# Revit family: QF_COMENDA_601682 AA_601682DDPS AA_CAT
name_source: partatom
category: Attrezzature speciali
units: mm (PartAtom-declared; Revit-internal decimal feet)

## family parameters
Basato su piano di lavoro = No
Condiviso = No
Numero OmniClass = 23.40.40.14
Punto di calcolo locali = No
Quota connettore circolare = Usa diametro
Sempre verticale = Sì
Taglio con vuoti quando caricato = No
Tipo di parte = Normale
Titolo OmniClass = Food Service Equipment

## types (3) — shared parameters
Altezza = 1960 mm  [stored 6.43045 ft]
Altezza allacciamento elettrico da pavimento finito = 360 mm
Altezza da terra raccordo acqua calda = 225 mm
Altezza dello scarico diretto acqua da pavimento finito = 225 mm
Corrente di funzionamento normale = 12 A
Diametro dello scarico diretto di acqua = 1 1/2"
Diametro raccordo acqua calda = 1"
Fase = 3
Frequenza = 50 Hz
Lunghezza = 620 mm  [stored 2.03412 ft]
Numero dei poli = 3
Peso netto = 0.00 kg
Potenza elettrica = 7500 W
Pressione minima acqua calda = 2000.0 Pa
Produttore = COMENDA
Profondità = 742 mm  [stored 2.43438 ft]
Protezione contro le sovracorrenti = 16 A
Temperatura raccomandata per acqua calda = 50 °C
Tensione = 400 V
URL = www.comenda.eu
zero-valued in all types: Prospetto di default

## per-type parameters (varying)
| type | Descrizione | Modello | URL catalogo |
| 601690/AA | MULTIPURPOSE WASHER 500X600 MM RACK SIZE WITH CRC | PFS90 R CRC |  |
| 601690DDPS/AA | MULTIPURPOSE WASHER 500X600 MM RACK SIZE WITH DRAIN PUMP, DETERGENT DOSING PUMP AND CRC | PFS90 R+ CRC | https://comenda.eu |
| 601690DD/AA | MULTIPURPOSE WASHER 500X600 MM RACK SIZE WITH DRAIN PUMP, DETERGENT DOSING PUMP AND CRC | PFS90 R DD CRC | https://comenda.eu |

note: [stored X ft] marks values corroborated as IEEE doubles in the binary element streams (Revit-internal decimal feet)

## geometry (parser evidence)
native form markers: Sweep x2
no freeform markers — native parametric forms only
